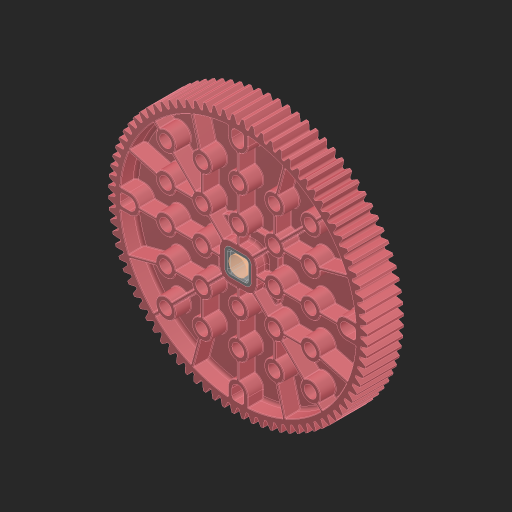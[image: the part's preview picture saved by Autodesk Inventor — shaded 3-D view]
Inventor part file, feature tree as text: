
AUTODESK INVENTOR PART (.ipt)
format: ipt  version: 2023 (Build 270158000, 158)  size: 5,307,904 bytes
history: native  units: in
note: dims shown in document units (in); Inventor stores cm internally (conversion verified against a paired STEP export)
features: other x3, sketch x1, extrude x1
ambient origin geometry x8: Origin, YZ Plane, XZ Plane, XY Plane, X Axis, Y Axis, Z Axis, Center Point
bodies: Solid1 (feature_tree), Solid2 (feature_tree)
feature tree (5):
  sketch  "Sketch1"  dims[d0=0.25in d1=0.3937in d2=0.0in]
  other  "Srf1"
  other  "276-7749-001_OVERMOLD Rev3_84T 24DP Gear Rev1_1:1"
  other  "276-7573-002 Rev7_2:1"
  extrude  "ExtrusionSrf1"  Depth=0.3937in TaperAngle=0.0deg
